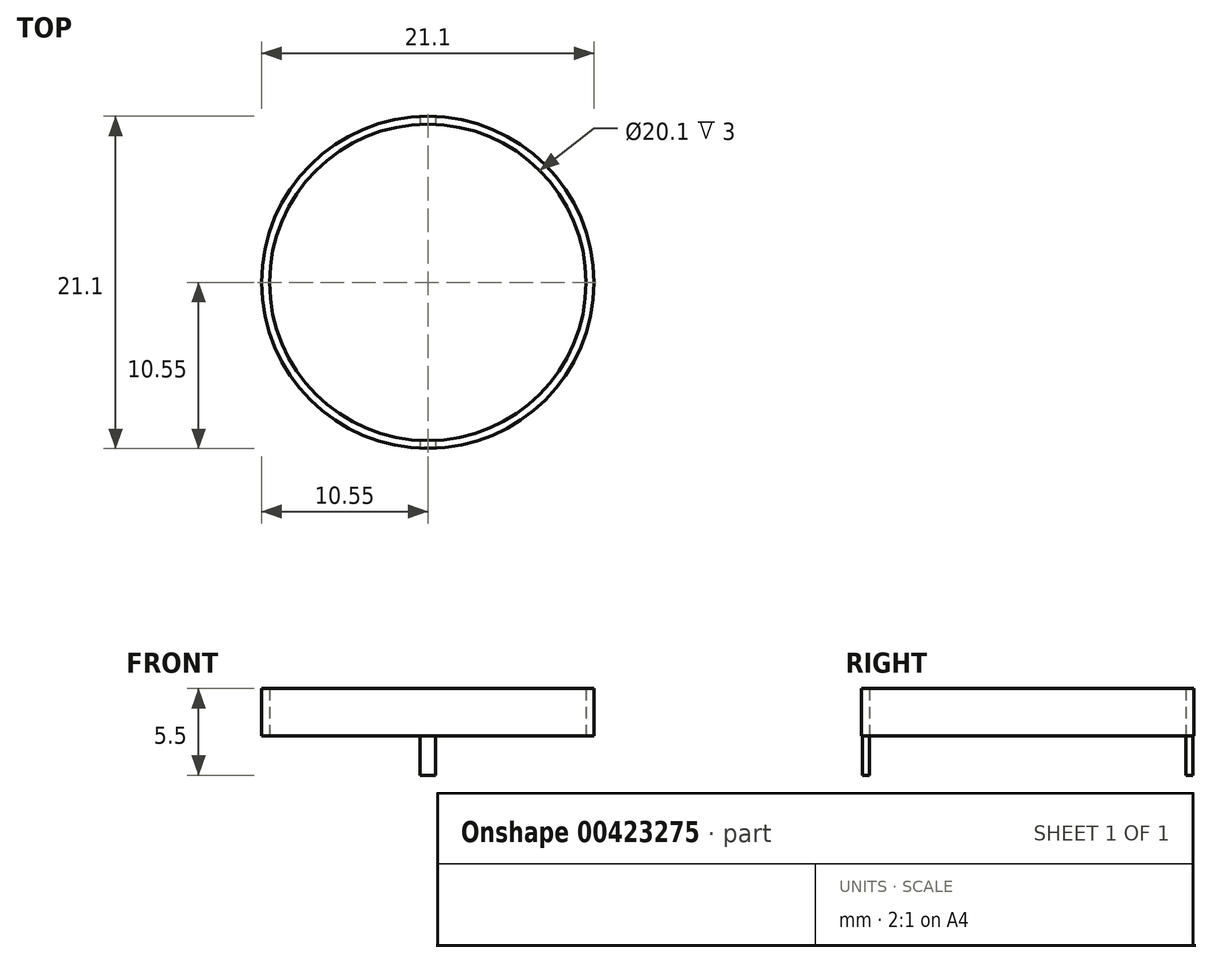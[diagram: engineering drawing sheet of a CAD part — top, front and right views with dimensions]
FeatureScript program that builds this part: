
annotation { "Feature Type Name" : "Feature", "Feature Type Description" : "" }
export const myFeature = defineFeature(function(context is Context, id is Id, definition is map)
    precondition{}
    {
        {
            var Q0;
            Q0=qCreatedBy(makeId("Top.planeOp"),FACE);
            var sketch = newSketch(context, id + "F0", { "sketchPlane" : qUnion([Q0])});
            skCircle(sketch, "E0", {"center": v(0, 0) * mm, "radius": 10.05 * mm});
            skCircle(sketch, "E1", {"center": v(0, 0) * mm, "radius": 10.55 * mm});
            skSolve(sketch);
        }
        {
            var Q0;
            Q0=makeQuery(id+"F0.imprint","IMPRINT",FACE,{"disambiguationData":[TD([[makeQuery(id+"F0.imprint","IMPRINT",EDGE,{"derivedFrom":sQuery(id+"F0.wireOp",EDGE,"E0")}),-1.0]])]});
            extrude(context, id + "F1", {"entities" : qUnion([Q0]), "depth" : 3 * mm});
        }
        {
            var Q0;
            Q0=qCreatedBy(makeId("Top.planeOp"),FACE);
            var sketch = newSketch(context, id + "F2", { "sketchPlane" : qUnion([Q0])});
            skLineSegment(sketch, "E2.bottom", {"start": v(0.5, 10.5) * mm, "end": v(-0.5, 10.5) * mm});
            skLineSegment(sketch, "E2.top", {"start": v(0.5, 10.05) * mm, "end": v(-0.5, 10.05) * mm});
            skLineSegment(sketch, "E2.left", {"start": v(0.5, 10.5) * mm, "end": v(0.5, 10.05) * mm});
            skLineSegment(sketch, "E2.right", {"start": v(-0.5, 10.5) * mm, "end": v(-0.5, 10.05) * mm});
            skSolve(sketch);
        }
        {
            var Q0;
            Q0=makeQuery(id+"F1.opExtrude","CAP_FACE",FACE,{"disambiguationData":[OSD([sQuery(id+"F0.wireOp",EDGE,"E0"),sQuery(id+"F0.wireOp",EDGE,"E1")])],"isStart":true});
            var sketch = newSketch(context, id + "F3", { "sketchPlane" : qUnion([Q0])});
            skLineSegment(sketch, "E3.bottom", {"start": v(0.5, 10.05) * mm, "end": v(-0.5, 10.05) * mm});
            skLineSegment(sketch, "E3.top", {"start": v(0.5, 10.5) * mm, "end": v(-0.5, 10.5) * mm});
            skLineSegment(sketch, "E3.left", {"start": v(0.5, 10.05) * mm, "end": v(0.5, 10.5) * mm});
            skLineSegment(sketch, "E3.right", {"start": v(-0.5, 10.05) * mm, "end": v(-0.5, 10.5) * mm});
            skSolve(sketch);
        }
        {
            var Q0;
            Q0=makeQuery(id+"F3.imprint","IMPRINT",FACE,{"disambiguationData":[TD([[makeQuery(id+"F3.imprint","IMPRINT",EDGE,{"derivedFrom":sQuery(id+"F3.wireOp",EDGE,"E3.top")}),1.0]])]});
            extrude(context, id + "F4", {"entities" : qUnion([Q0]), "operationType" : NewBodyOperationType.ADD, "depth" : 2.5 * mm});
        }
        {
            var Q0;
            Q0=makeQuery(id+"F2.imprint","IMPRINT",FACE,{"disambiguationData":[TD([[makeQuery(id+"F2.imprint","IMPRINT",EDGE,{"derivedFrom":sQuery(id+"F2.wireOp",EDGE,"E2.bottom")}),1.0]])]});
            extrude(context, id + "F5", {"entities" : qUnion([Q0]), "operationType" : NewBodyOperationType.ADD, "oppositeDirection" : true, "depth" : 2.5 * mm});
        }
    });
